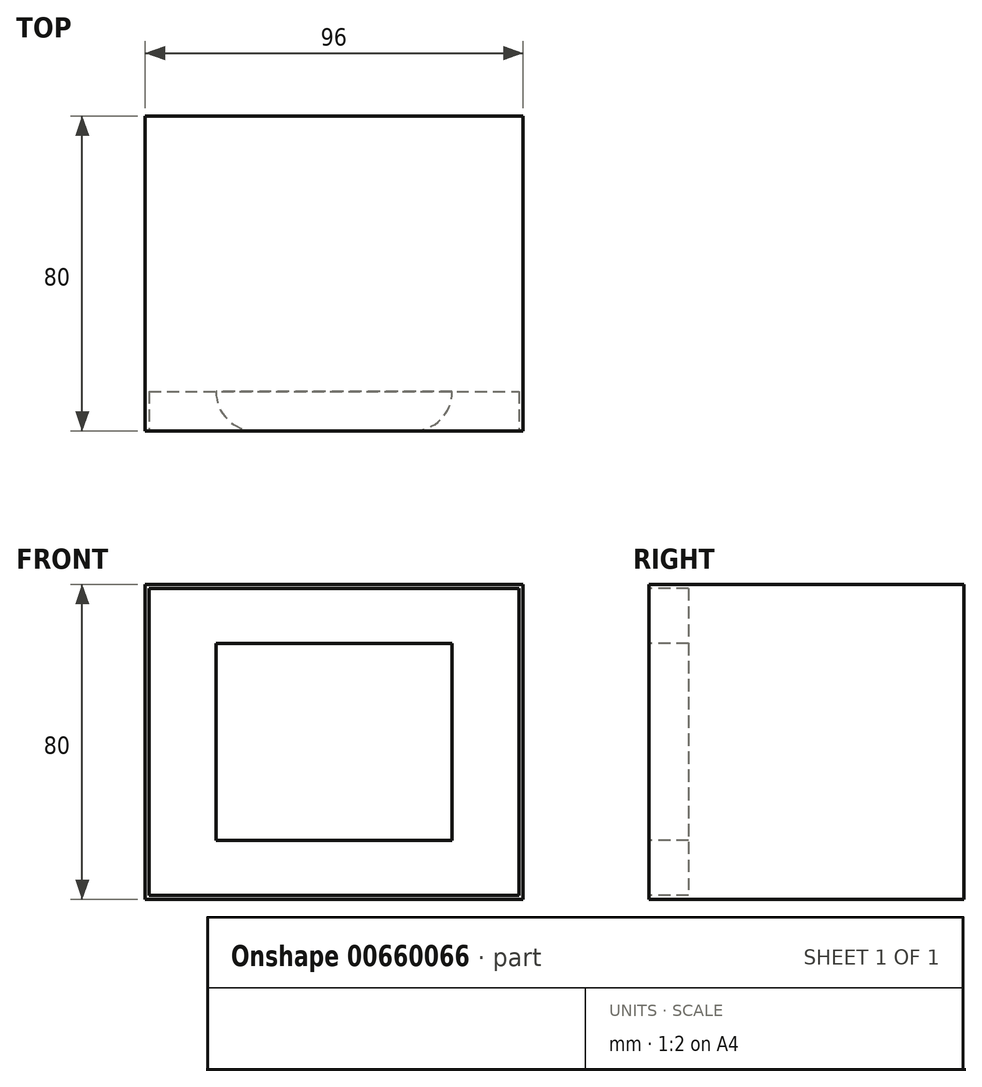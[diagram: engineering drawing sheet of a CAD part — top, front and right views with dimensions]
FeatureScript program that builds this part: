
annotation { "Feature Type Name" : "Feature", "Feature Type Description" : "" }
export const myFeature = defineFeature(function(context is Context, id is Id, definition is map)
    precondition{}
    {
        {
            var Q0;
            Q0=qCreatedBy(makeId("Top.planeOp"),FACE);
            var sketch = newSketch(context, id + "F0", { "sketchPlane" : qUnion([Q0])});
            skLineSegment(sketch, "E0.bottom", {"start": v(-48, 40) * mm, "end": v(48, 40) * mm});
            skLineSegment(sketch, "E0.top", {"start": v(-48, -40) * mm, "end": v(48, -40) * mm});
            skLineSegment(sketch, "E0.left", {"start": v(-48, 40) * mm, "end": v(-48, -40) * mm});
            skLineSegment(sketch, "E0.right", {"start": v(48, 40) * mm, "end": v(48, -40) * mm});
            skPoint(sketch, "E0.middle", {"position": v(0, 0) * mm});
            skSolve(sketch);
        }
        {
            var Q0;
            Q0=makeQuery(id+"F0.imprint","IMPRINT",FACE,{"disambiguationData":[TD([[makeQuery(id+"F0.imprint","IMPRINT",EDGE,{"derivedFrom":sQuery(id+"F0.wireOp",EDGE,"E0.bottom")}),-1.0]])]});
            extrude(context, id + "F1", {"entities" : qUnion([Q0]), "depth" : 80 * mm});
        }
        {
            var Q0;
            Q0=makeQuery(id+"F1.opExtrude","SWEPT_FACE",FACE,{"disambiguationData":[OSD([sQuery(id+"F0.wireOp",EDGE,"E0.top")])]});
            var sketch = newSketch(context, id + "F2", { "sketchPlane" : qUnion([Q0])});
            skLineSegment(sketch, "E1.0", {"start": v(-47, 1) * mm, "end": v(47, 1) * mm});
            skLineSegment(sketch, "E1.1", {"start": v(-47, 79) * mm, "end": v(-47, 1) * mm});
            skLineSegment(sketch, "E1.2", {"start": v(47, 79) * mm, "end": v(-47, 79) * mm});
            skLineSegment(sketch, "E1.3", {"start": v(47, 1) * mm, "end": v(47, 79) * mm});
            skLineSegment(sketch, "E2.bottom", {"start": v(30, 65) * mm, "end": v(-30, 65) * mm});
            skLineSegment(sketch, "E2.top", {"start": v(30, 15) * mm, "end": v(-30, 15) * mm});
            skLineSegment(sketch, "E2.left", {"start": v(30, 65) * mm, "end": v(30, 15) * mm});
            skLineSegment(sketch, "E2.right", {"start": v(-30, 65) * mm, "end": v(-30, 15) * mm});
            skPoint(sketch, "E2.middle", {"position": v(0, 40) * mm});
            skPoint(sketch, "E2.middle.positionSnap0", {"position": v(0, 80) * mm});
            skPoint(sketch, "E2.middle.positionSnap1", {"position": v(47, 40) * mm});
            skPoint(sketch, "E2.centerSnap0", {"position": v(0, 80) * mm});
            skPoint(sketch, "E2.centerSnap1", {"position": v(47, 40) * mm});
            skSolve(sketch);
        }
        {
            var Q0;
            Q0=makeQuery(id+"F2.imprint","IMPRINT",FACE,{"disambiguationData":[TD([[makeQuery(id+"F2.imprint","IMPRINT",EDGE,{"derivedFrom":sQuery(id+"F2.wireOp",EDGE,"E1.0")}),1.0]])]});
            extrude(context, id + "F3", {"entities" : qUnion([Q0]), "operationType" : NewBodyOperationType.REMOVE, "oppositeDirection" : true, "depth" : 10 * mm});
        }
        {
            var Q0;
            Q0=makeQuery(id+"F3.boolean.opBoolean","COPY",EDGE,{"derivedFrom":makeQuery(id+"F3.opExtrude","CAP_EDGE",EDGE,{"disambiguationData":[OSD([sQuery(id+"F2.wireOp",EDGE,"E2.left")])],"isStart":true})});
            var Q1;
            Q1=makeQuery(id+"F3.boolean.opBoolean","COPY",EDGE,{"derivedFrom":makeQuery(id+"F3.opExtrude","CAP_EDGE",EDGE,{"disambiguationData":[OSD([sQuery(id+"F2.wireOp",EDGE,"E2.right")])],"isStart":true})});
            fillet(context, id + "F4", {"entities" : qUnion([Q0, Q1]), "radius" : 10 * mm, "tangentPropagation" : true, "allowEdgeOverflow" : false});
        }
    });
